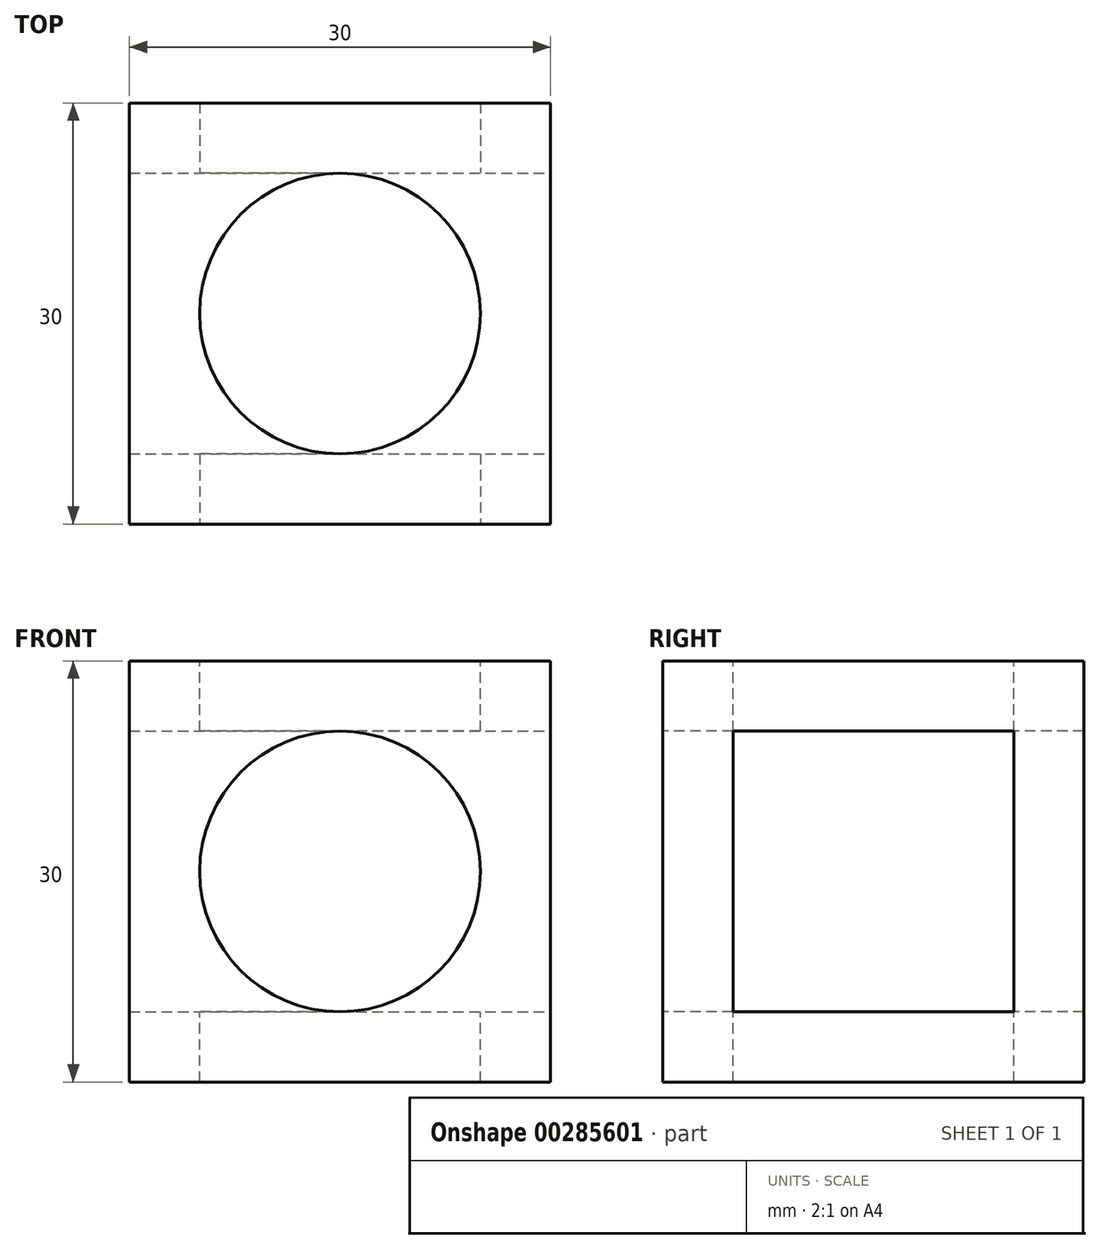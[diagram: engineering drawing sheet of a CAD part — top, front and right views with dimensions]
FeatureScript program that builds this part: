
annotation { "Feature Type Name" : "Feature", "Feature Type Description" : "" }
export const myFeature = defineFeature(function(context is Context, id is Id, definition is map)
    precondition{}
    {
        {
            var Q0;
            Q0=qCreatedBy(makeId("Front.planeOp"),FACE);
            var sketch = newSketch(context, id + "F0", { "sketchPlane" : qUnion([Q0])});
            skLineSegment(sketch, "E0.bottom", {"start": v(15, 15) * mm, "end": v(-15, 15) * mm});
            skLineSegment(sketch, "E0.top", {"start": v(15, -15) * mm, "end": v(-15, -15) * mm});
            skLineSegment(sketch, "E0.left", {"start": v(15, 15) * mm, "end": v(15, -15) * mm});
            skLineSegment(sketch, "E0.right", {"start": v(-15, 15) * mm, "end": v(-15, -15) * mm});
            skPoint(sketch, "E0.middle", {"position": v(0, 0) * mm});
            skSolve(sketch);
        }
        {
            var Q0;
            Q0=makeQuery(id+"F0.imprint","IMPRINT",FACE,{"disambiguationData":[TD([[makeQuery(id+"F0.imprint","IMPRINT",EDGE,{"derivedFrom":sQuery(id+"F0.wireOp",EDGE,"E0.bottom")}),1.0]])]});
            extrude(context, id + "F1", {"entities" : qUnion([Q0]), "depth" : 30 * mm});
        }
        {
            var Q0;
            Q0=makeQuery(id+"F1.opExtrude","CAP_FACE",FACE,{"disambiguationData":[OSD([sQuery(id+"F0.wireOp",EDGE,"E0.bottom"),sQuery(id+"F0.wireOp",EDGE,"E0.top"),sQuery(id+"F0.wireOp",EDGE,"E0.left"),sQuery(id+"F0.wireOp",EDGE,"E0.right")])],"isStart":false});
            var sketch = newSketch(context, id + "F2", { "sketchPlane" : qUnion([Q0])});
            skCircle(sketch, "E1", {"center": v(0, 0) * mm, "radius": 10 * mm});
            skSolve(sketch);
        }
        {
            var Q0;
            Q0 = qSketchRegion(id + "F2", true);
            extrude(context, id + "F3", {"entities" : qUnion([Q0]), "operationType" : NewBodyOperationType.REMOVE, "endBound" : BoundingType.THROUGH_ALL, "oppositeDirection" : true, "depth" : 25 * mm});
        }
        {
            var Q0;
            Q0=makeQuery(id+"F1.opExtrude","SWEPT_FACE",FACE,{"disambiguationData":[OSD([sQuery(id+"F0.wireOp",EDGE,"E0.bottom")])]});
            var sketch = newSketch(context, id + "F4", { "sketchPlane" : qUnion([Q0])});
            skCircle(sketch, "E2", {"center": v(0, -15) * mm, "radius": 10 * mm});
            skPoint(sketch, "E2.centerSnap0", {"position": v(15, -15) * mm});
            skSolve(sketch);
        }
        {
            var Q0;
            Q0 = qSketchRegion(id + "F4", true);
            extrude(context, id + "F5", {"entities" : qUnion([Q0]), "operationType" : NewBodyOperationType.REMOVE, "endBound" : BoundingType.THROUGH_ALL, "oppositeDirection" : true, "depth" : 25 * mm});
        }
        {
            var Q0;
            Q0=makeQuery(id+"F1.opExtrude","SWEPT_FACE",FACE,{"disambiguationData":[OSD([sQuery(id+"F0.wireOp",EDGE,"E0.left")])]});
            var sketch = newSketch(context, id + "F6", { "sketchPlane" : qUnion([Q0])});
            skLineSegment(sketch, "E3.bottom", {"start": v(-5, 10) * mm, "end": v(-25, 10) * mm});
            skLineSegment(sketch, "E3.top", {"start": v(-5, -10) * mm, "end": v(-25, -10) * mm});
            skLineSegment(sketch, "E3.left", {"start": v(-5, 10) * mm, "end": v(-5, -10) * mm});
            skLineSegment(sketch, "E3.right", {"start": v(-25, 10) * mm, "end": v(-25, -10) * mm});
            skPoint(sketch, "E3.middle", {"position": v(-15, 0) * mm});
            skPoint(sketch, "E3.middle.positionSnap0", {"position": v(-15, 15) * mm});
            skPoint(sketch, "E3.centerSnap0", {"position": v(-15, 15) * mm});
            skSolve(sketch);
        }
        {
            var Q0;
            Q0 = qSketchRegion(id + "F6", true);
            extrude(context, id + "F7", {"entities" : qUnion([Q0]), "operationType" : NewBodyOperationType.REMOVE, "endBound" : BoundingType.THROUGH_ALL, "oppositeDirection" : true, "depth" : 25 * mm});
        }
    });
